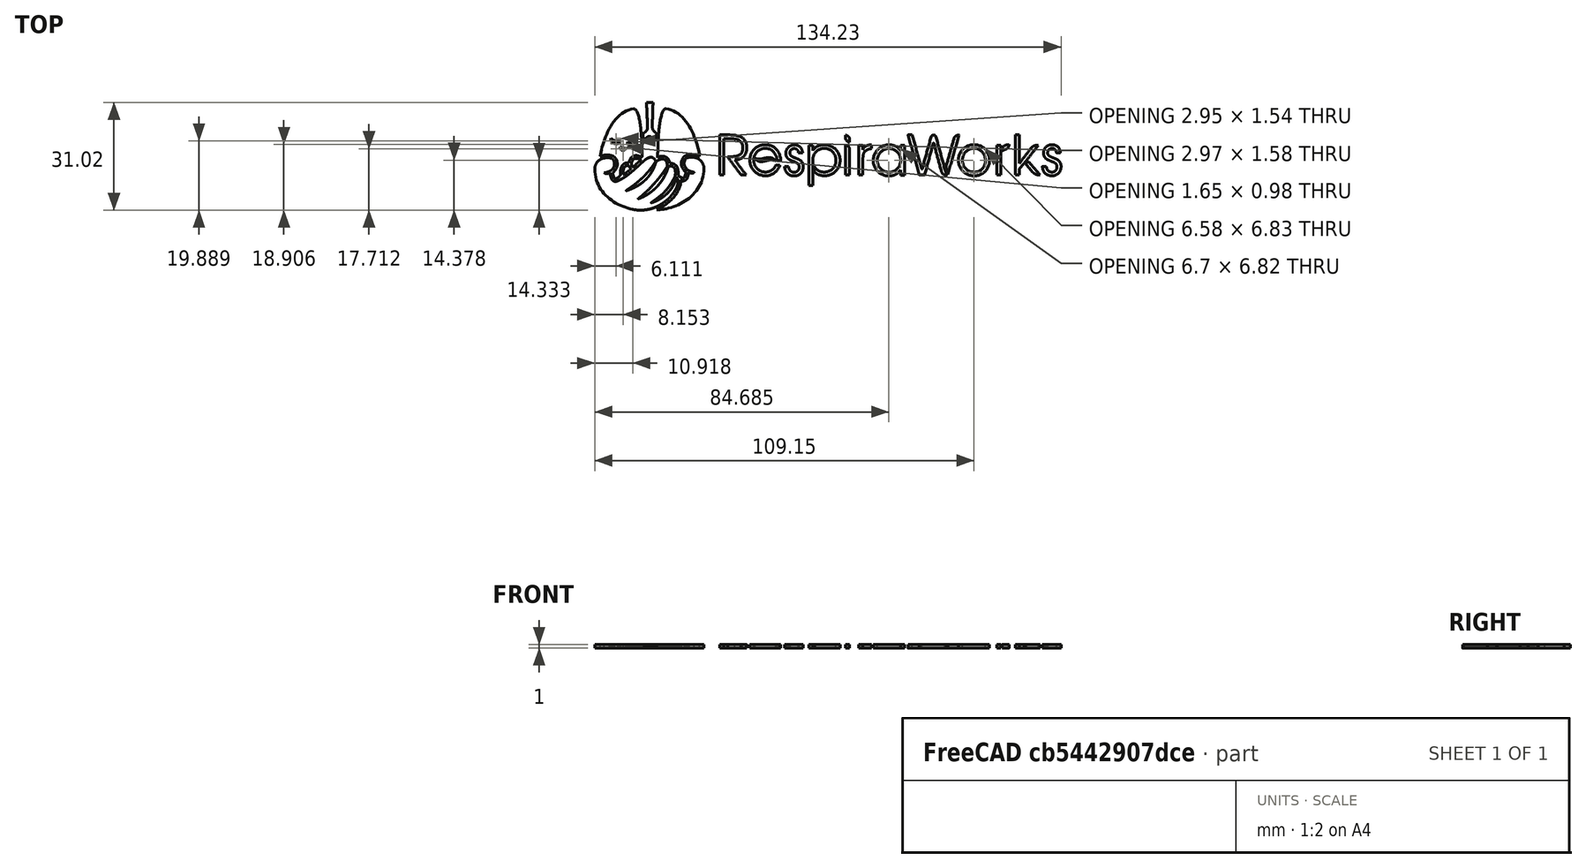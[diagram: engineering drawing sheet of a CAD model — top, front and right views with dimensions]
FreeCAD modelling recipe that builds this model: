
FCSTD DOCUMENT  (FreeCAD 0.18R4 (GitTag))
Label: logo-V2
License: All rights reserved
LicenseURL: http://en.wikipedia.org/wiki/All_rights_reserved
objects: Part::Feature×38, Part::Extrusion×29, Part::MultiFuse×7, Part::Mirroring×3, Part::Cut×2, Part::FeaturePython×1
note: 80 computed .brp shape members not serialized (recipe doc carries the construction recipe); baked Part::Feature solids carry a one-line shape summary decoded from their .brp

FEATURE [Part::Feature] path428  label="path428na"
  shape: bbox 3.153 x 1.741 x 2e-07 mm, 0 faces, 0 solids (baked)
FEATURE [Part::Feature] path430  label="path430na"
  shape: bbox 1.76 x 1.081 x 2e-07 mm, 0 faces, 0 solids (baked)
FEATURE [Part::Feature] path432  label="path432na"
  shape: bbox 3.134 x 1.688 x 2e-07 mm, 0 faces, 0 solids (baked)
FEATURE [Part::Feature] path434  label="path434na"
  shape: bbox 33.04 x 16.98 x 2e-07 mm, 0 faces, 0 solids (baked)
FEATURE [Part::Feature] path434001  label="path434001na"
  shape: bbox 2.744 x 2.564 x 2e-07 mm, 0 faces, 0 solids (baked)
FEATURE [Part::Feature] path434002  label="path434002na"
  shape: bbox 2.22 x 2.625 x 2e-07 mm, 0 faces, 0 solids (baked)
FEATURE [Part::Feature] path434003  label="path434003na"
  shape: bbox 23.98 x 15.22 x 2e-07 mm, 0 faces, 0 solids (baked)
FEATURE [Part::Feature] path434004  label="path434004na"
  shape: bbox 13.56 x 15.09 x 2e-07 mm, 0 faces, 0 solids (baked)
FEATURE [Part::Feature] path446001  label="path446001na"
  shape: bbox 2e-07 x 2.291 x 2e-07 mm, 0 faces, 0 solids (baked)
FEATURE [Part::Feature] Face
  shape: bbox 3.58 x 8.758 x 2e-07 mm, 1 faces, 0 solids (baked)
FEATURE [Part::Feature] Face001
  shape: bbox 6.699 x 6.927 x 2e-07 mm, 1 faces, 0 solids (baked)
FEATURE [Part::Feature] Face002
  shape: bbox 9.112 x 9.183 x 2e-07 mm, 1 faces, 0 solids (baked)
FEATURE [Part::Feature] Face003
  shape: bbox 5.342 x 8.932 x 2e-07 mm, 1 faces, 0 solids (baked)
FEATURE [Part::Feature] Face004
  shape: bbox 1.156 x 8.557 x 2e-07 mm, 1 faces, 0 solids (baked)
FEATURE [Part::Feature] Face005
  shape: bbox 1.156 x 1.971 x 2e-07 mm, 1 faces, 0 solids (baked)
FEATURE [Part::Feature] Face006
  shape: bbox 9.051 x 12.05 x 2e-07 mm, 1 faces, 0 solids (baked)
FEATURE [Part::Feature] Face007
  shape: bbox 9.142 x 9.001 x 2e-07 mm, 1 faces, 0 solids (baked)
FEATURE [Part::Feature] Face008
  shape: bbox 5.94 x 1.154 x 2e-07 mm, 1 faces, 0 solids (baked)
FEATURE [Part::Feature] Face009
  shape: bbox 7.842 x 11.56 x 2e-07 mm, 1 faces, 0 solids (baked)
FEATURE [Part::Feature] Face010
  shape: bbox 5.363 x 9.106 x 2e-07 mm, 1 faces, 0 solids (baked)
FEATURE [Part::Feature] Face011
  shape: bbox 6.583 x 6.832 x 2e-07 mm, 1 faces, 0 solids (baked)
FEATURE [Part::Feature] Face012
  shape: bbox 8.927 x 8.959 x 2e-07 mm, 1 faces, 0 solids (baked)
FEATURE [Part::Feature] Face013
  shape: bbox 1.995 x 1.775 x 2e-07 mm, 1 faces, 0 solids (baked)
FEATURE [Part::Feature] Face014
  shape: bbox 1.159 x 8.554 x 2e-07 mm, 1 faces, 0 solids (baked)
FEATURE [Part::Feature] Face015
  shape: bbox 6.567 x 11.56 x 2e-07 mm, 1 faces, 0 solids (baked)
FEATURE [Part::Feature] Face016
  shape: bbox 4.239 x 3.757 x 2e-07 mm, 1 faces, 0 solids (baked)
FEATURE [Part::Feature] Face017
  shape: bbox 3.769 x 11.29 x 2e-07 mm, 1 faces, 0 solids (baked)
FEATURE [Part::Feature] Face018
  shape: bbox 11.13 x 11.6 x 2e-07 mm, 1 faces, 0 solids (baked)
FEATURE [Part::Feature] Face019
  shape: bbox 23.98 x 15.22 x 2e-07 mm, 1 faces, 0 solids (baked)
FEATURE [Part::Feature] Face020
  shape: bbox 13.56 x 15.09 x 2e-07 mm, 1 faces, 0 solids (baked)
FEATURE [Part::Feature] Face021
  shape: bbox 2.22 x 2.625 x 2e-07 mm, 1 faces, 0 solids (baked)
FEATURE [Part::Feature] Face022
  shape: bbox 2.744 x 2.564 x 2e-07 mm, 1 faces, 0 solids (baked)
FEATURE [Part::Feature] Face023
  shape: bbox 4.011 x 10.85 x 2e-07 mm, 1 faces, 0 solids (baked)
FEATURE [Part::Feature] Face024
  shape: bbox 12.13 x 20.08 x 2e-07 mm, 1 faces, 0 solids (baked)
FEATURE [Part::Feature] Face025
  shape: bbox 3.134 x 1.688 x 2e-07 mm, 1 faces, 0 solids (baked)
FEATURE [Part::Feature] Face026
  shape: bbox 1.76 x 1.081 x 2e-07 mm, 1 faces, 0 solids (baked)
FEATURE [Part::Feature] Face027
  shape: bbox 3.153 x 1.741 x 2e-07 mm, 1 faces, 0 solids (baked)
FEATURE [Part::Feature] Face028
  shape: bbox 12.09 x 20.21 x 2e-07 mm, 1 faces, 0 solids (baked)
FEATURE [Part::Extrusion] Extrude  label="p-m-r1"
  Base = -> Face
  Dir = (0,0,-1)
  DirMode = 2
  FaceMakerClass = Part::FaceMakerBullseye
  LengthFwd = 1
  LengthRev = 0
  Solid = false
  Symmetric = false
FEATURE [Part::Extrusion] Extrude001  label="n-a"
  Base = -> Face001
  Dir = (0,0,1)
  DirMode = 2
  FaceMakerClass = Part::FaceMakerBullseye
  LengthFwd = 1
  LengthRev = 0
  Solid = false
  Symmetric = false
FEATURE [Part::Extrusion] Extrude002  label="p-m-a"
  Base = -> Face002
  Dir = (0,0,-1)
  DirMode = 2
  FaceMakerClass = Part::FaceMakerBullseye
  LengthFwd = 1
  LengthRev = 0
  Solid = false
  Symmetric = false
FEATURE [Part::Extrusion] Extrude003  label="p-m-s1"
  Base = -> Face003
  Dir = (0,0,-1)
  DirMode = 2
  FaceMakerClass = Part::FaceMakerBullseye
  LengthFwd = 1
  LengthRev = 0
  Solid = false
  Symmetric = false
FEATURE [Part::Extrusion] Extrude004  label="p-m-i-2"
  Base = -> Face004
  Dir = (0,0,-1)
  DirMode = 2
  FaceMakerClass = Part::FaceMakerBullseye
  LengthFwd = 1
  LengthRev = 0
  Solid = false
  Symmetric = false
FEATURE [Part::Extrusion] Extrude005  label="p-m-i-1"
  Base = -> Face005
  Dir = (0,0,-1)
  DirMode = 2
  FaceMakerClass = Part::FaceMakerBullseye
  LengthFwd = 1
  LengthRev = 0
  Solid = false
  Symmetric = false
FEATURE [Part::Extrusion] Extrude006  label="p-p"
  Base = -> Face006
  Dir = (0,0,1)
  DirMode = 2
  FaceMakerClass = Part::FaceMakerBullseye
  LengthFwd = 1
  LengthRev = 0
  Solid = false
  Symmetric = false
FEATURE [Part::Extrusion] Extrude007  label="p-e-1"
  Base = -> Face007
  Dir = (0,0,1)
  DirMode = 2
  FaceMakerClass = Part::FaceMakerBullseye
  LengthFwd = 1
  LengthRev = 0
  Solid = false
  Symmetric = false
FEATURE [Part::Extrusion] Extrude008  label="p-m-e-2"
  Base = -> Face008
  Dir = (0,0,-1)
  DirMode = 2
  FaceMakerClass = Part::FaceMakerBullseye
  LengthFwd = 1
  LengthRev = 0
  Solid = false
  Symmetric = false
FEATURE [Part::Extrusion] Extrude009  label="p-m-R"
  Base = -> Face009
  Dir = (0,0,-1)
  DirMode = 2
  FaceMakerClass = Part::FaceMakerBullseye
  LengthFwd = 1
  LengthRev = 0
  Solid = false
  Symmetric = false
FEATURE [Part::Extrusion] Extrude010  label="p-m-s2"
  Base = -> Face010
  Dir = (0,0,-1)
  DirMode = 2
  FaceMakerClass = Part::FaceMakerBullseye
  LengthFwd = 1
  LengthRev = 0
  Solid = false
  Symmetric = false
FEATURE [Part::Extrusion] Extrude011  label="n-o"
  Base = -> Face011
  Dir = (0,0,1)
  DirMode = 2
  FaceMakerClass = Part::FaceMakerBullseye
  LengthFwd = 1
  LengthRev = 0
  Solid = false
  Symmetric = false
FEATURE [Part::Extrusion] Extrude012  label="p-m-o"
  Base = -> Face012
  Dir = (0,0,-1)
  DirMode = 2
  FaceMakerClass = Part::FaceMakerBullseye
  LengthFwd = 1
  LengthRev = 0
  Solid = false
  Symmetric = false
FEATURE [Part::Extrusion] Extrude013  label="p-r2-2"
  Base = -> Face013
  Dir = (0,0,1)
  DirMode = 2
  FaceMakerClass = Part::FaceMakerBullseye
  LengthFwd = 1
  LengthRev = 0
  Solid = false
  Symmetric = false
FEATURE [Part::Extrusion] Extrude014  label="p-r2-1"
  Base = -> Face014
  Dir = (0,0,1)
  DirMode = 2
  FaceMakerClass = Part::FaceMakerBullseye
  LengthFwd = 1
  LengthRev = 0
  Solid = false
  Symmetric = false
FEATURE [Part::Extrusion] Extrude015  label="p-k-1"
  Base = -> Face015
  Dir = (0,0,1)
  DirMode = 2
  FaceMakerClass = Part::FaceMakerBullseye
  LengthFwd = 1
  LengthRev = 0
  Solid = false
  Symmetric = false
FEATURE [Part::Extrusion] Extrude016  label="p-k-2"
  Base = -> Face016
  Dir = (0,0,1)
  DirMode = 2
  FaceMakerClass = Part::FaceMakerBullseye
  LengthFwd = 1
  LengthRev = 0
  Solid = false
  Symmetric = false
FEATURE [Part::Extrusion] Extrude017  label="p-W-2"
  Base = -> Face017
  Dir = (0,0,1)
  DirMode = 2
  FaceMakerClass = Part::FaceMakerBullseye
  LengthFwd = 1
  LengthRev = 0
  Solid = false
  Symmetric = false
FEATURE [Part::Extrusion] Extrude018  label="p-W-1"
  Base = -> Face018
  Dir = (0,0,1)
  DirMode = 2
  FaceMakerClass = Part::FaceMakerBullseye
  LengthFwd = 1
  LengthRev = 0
  Solid = false
  Symmetric = false
FEATURE [Part::Extrusion] Extrude019  label="p-m-LeftHand"
  Base = -> Face019
  Dir = (0,0,-1)
  DirMode = 2
  FaceMakerClass = Part::FaceMakerBullseye
  LengthFwd = 1
  LengthRev = 0
  Solid = false
  Symmetric = false
FEATURE [Part::Extrusion] Extrude020  label="p-m-RightHand"
  Base = -> Face020
  Dir = (0,0,-1)
  DirMode = 2
  FaceMakerClass = Part::FaceMakerBullseye
  LengthFwd = 1
  LengthRev = 0
  Solid = false
  Symmetric = false
FEATURE [Part::Extrusion] Extrude021  label="p-m-LeftFinger"
  Base = -> Face021
  Dir = (0,0,-1)
  DirMode = 2
  FaceMakerClass = Part::FaceMakerBullseye
  LengthFwd = 1
  LengthRev = 0
  Solid = false
  Symmetric = false
FEATURE [Part::Extrusion] Extrude022  label="p-m-RightFinger"
  Base = -> Face022
  Dir = (0,0,-1)
  DirMode = 2
  FaceMakerClass = Part::FaceMakerBullseye
  LengthFwd = 1
  LengthRev = 0
  Solid = false
  Symmetric = false
FEATURE [Part::Extrusion] Extrude023  label="p-Trachea"
  Base = -> Face023
  Dir = (0,0,1)
  DirMode = 2
  FaceMakerClass = Part::FaceMakerBullseye
  LengthFwd = 1
  LengthRev = 0
  Solid = false
  Symmetric = false
FEATURE [Part::Extrusion] Extrude024  label="p-m-RightLung"
  Base = -> Face024
  Dir = (0,0,-1)
  DirMode = 2
  FaceMakerClass = Part::FaceMakerBullseye
  LengthFwd = 1
  LengthRev = 0
  Solid = false
  Symmetric = false
FEATURE [Part::Extrusion] Extrude025  label="n-m-RightEye"
  Base = -> Face025
  Dir = (0,0,-1)
  DirMode = 2
  FaceMakerClass = Part::FaceMakerBullseye
  LengthFwd = 1
  LengthRev = 0
  Solid = false
  Symmetric = false
FEATURE [Part::Extrusion] Extrude026  label="n-m-Mouth"
  Base = -> Face026
  Dir = (0,0,-1)
  DirMode = 2
  FaceMakerClass = Part::FaceMakerBullseye
  LengthFwd = 1
  LengthRev = 0
  Solid = false
  Symmetric = false
FEATURE [Part::Extrusion] Extrude027  label="n-m-LeftEye"
  Base = -> Face027
  Dir = (0,0,-1)
  DirMode = 2
  FaceMakerClass = Part::FaceMakerBullseye
  LengthFwd = 1
  LengthRev = 0
  Solid = false
  Symmetric = false
FEATURE [Part::Extrusion] Extrude028  label="p-LeftLung"
  Base = -> Face028
  Dir = (0,0,1)
  DirMode = 2
  FaceMakerClass = Part::FaceMakerBullseye
  LengthFwd = 1
  LengthRev = 0
  Solid = false
  Symmetric = false
FEATURE [Part::MultiFuse] Fusion  label="n-m-Face"
  Shapes = -> [Extrude027,Extrude026,Extrude025]
FEATURE [Part::Mirroring] Part__Mirroring  label="nLogo (Mirror #1)"
  Base = (0,0,0)
  Normal = (0,0,1)
  Source = -> Fusion
FEATURE [Part::MultiFuse] Fusion001  label="p-m-Lungs"
  Shapes = -> [Extrude024,Extrude022,Extrude021,Extrude020,Extrude019]
FEATURE [Part::Mirroring] Part__Mirroring001  label="p-m-Lungs (Mirror #2)"
  Base = (0,0,0)
  Normal = (0,0,1)
  Source = -> Fusion001
FEATURE [Part::MultiFuse] Fusion002  label="pLogo"
  Shapes = -> [Part__Mirroring001,Extrude028,Extrude023]
FEATURE [Part::Cut] Cut  label="Logo"
  Base = -> Fusion002
  Tool = -> Part__Mirroring
FEATURE [Part::MultiFuse] Fusion003  label="p-m-text"
  Shapes = -> [Extrude012,Extrude010,Extrude009,Extrude008,Extrude005,Extrude004,Extrude003,Extrude002,Extrude]
FEATURE [Part::Mirroring] Part__Mirroring002  label="p-m-text (Mirror #3)"
  Base = (0,0,0)
  Normal = (0,0,1)
  Source = -> Fusion003
FEATURE [Part::MultiFuse] Fusion004  label="pText"
  Shapes = -> [Part__Mirroring002,Extrude018,Extrude017,Extrude016,Extrude015,Extrude014,Extrude013,Extrude007,Extrude006]
FEATURE [Part::MultiFuse] Fusion005  label="nText"
  Shapes = -> [Extrude011,Extrude001]
FEATURE [Part::Cut] Cut001  label="Text"
  Base = -> Fusion004
  Tool = -> Fusion005
FEATURE [Part::MultiFuse] Fusion006  label="RW-LogoPlusText-Extrude-1mm"
  Shapes = -> [Cut,Cut001]
FEATURE [Part::FeaturePython] Clone  label="RW-LogoPlusText-Extrude-ScaledClone"  # Draft clone (typed FeaturePython)
  AttacherType = Attacher::AttachEngine3D
  Fuse = false
  Objects = -> [Fusion006]
  Scale = (1,1,1)
